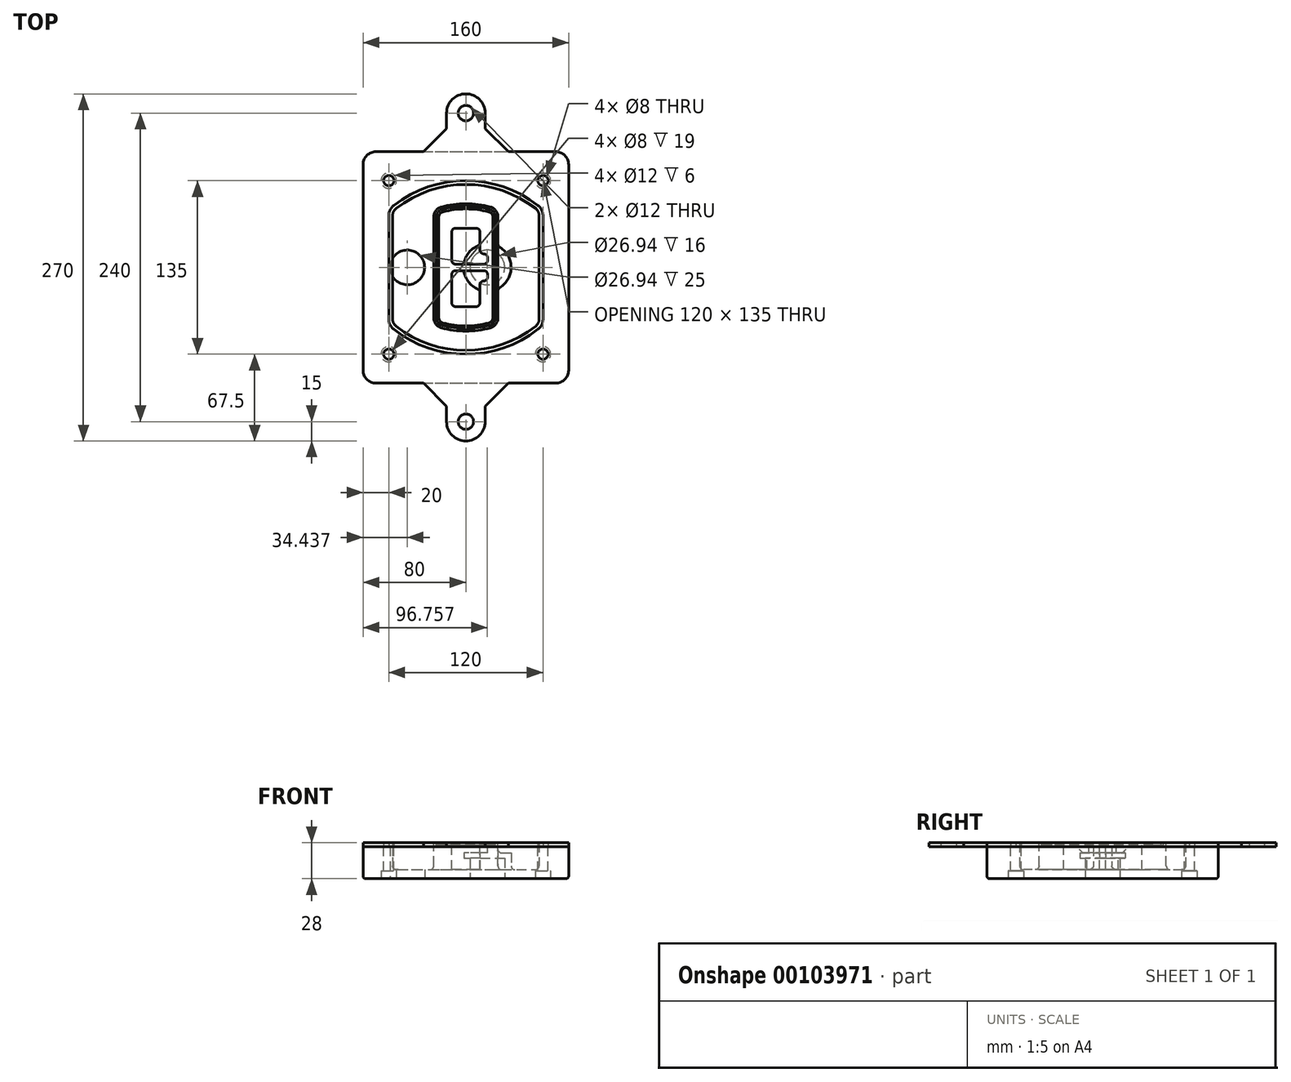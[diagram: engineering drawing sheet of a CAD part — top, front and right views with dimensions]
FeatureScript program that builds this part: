
annotation { "Feature Type Name" : "Feature", "Feature Type Description" : "" }
export const myFeature = defineFeature(function(context is Context, id is Id, definition is map)
    precondition{}
    {
        {
            var Q0;
            Q0=qCreatedBy(makeId("Top.planeOp"),FACE);
            var sketch = newSketch(context, id + "F0", { "sketchPlane" : qUnion([Q0])});
            skPoint(sketch, "E0.rect.middle", {"position": v(0, 0) * mm});
            skLineSegment(sketch, "E1.bottom", {"start": v(-70, -90) * mm, "end": v(70, -90) * mm});
            skLineSegment(sketch, "E1.top", {"start": v(-70, 90) * mm, "end": v(70, 90) * mm});
            skLineSegment(sketch, "E1.left", {"start": v(-80, -80) * mm, "end": v(-80, 80) * mm});
            skLineSegment(sketch, "E1.right", {"start": v(80, -80) * mm, "end": v(80, 80) * mm});
            skLineSegment(sketch, "E2", {"start": v(-80, 90) * mm, "end": v(80, -90) * mm, "construction": true});
            skLineSegment(sketch, "E3", {"start": v(80, 90) * mm, "end": v(-80, -90) * mm, "construction": true});
            skCircle(sketch, "E4", {"center": v(-60, 67.5) * mm, "radius": 4 * mm});
            skCircle(sketch, "E5", {"center": v(60, 67.5) * mm, "radius": 4 * mm});
            skCircle(sketch, "E6", {"center": v(60, -67.5) * mm, "radius": 4 * mm});
            skCircle(sketch, "E7", {"center": v(-60, -67.5) * mm, "radius": 4 * mm});
            skLineSegment(sketch, "E8", {"start": v(-60, 67.5) * mm, "end": v(60, 67.5) * mm, "construction": true});
            skLineSegment(sketch, "E9", {"start": v(60, 67.5) * mm, "end": v(60, -67.5) * mm, "construction": true});
            skLineSegment(sketch, "E10", {"start": v(60, -67.5) * mm, "end": v(-60, -67.5) * mm, "construction": true});
            skLineSegment(sketch, "E11", {"start": v(-60, -67.5) * mm, "end": v(-60, 67.5) * mm, "construction": true});
            skLineSegment(sketch, "E12", {"start": v(-60, 40.3) * mm, "end": v(-60, -40.3) * mm});
            skLineSegment(sketch, "E13", {"start": v(60, 40.3) * mm, "end": v(60, -40.3) * mm});
            skArc(sketch, "E14", {"start": v(56.15, 48.18) * mm, "mid": v(0, 67.5) * mm, "end": v(-56.15, 48.18) * mm});
            skArc(sketch, "E15", {"start": v(-56.15, -48.18) * mm, "mid": v(0, -67.5) * mm, "end": v(56.15, -48.18) * mm});
            skLineSegment(sketch, "E16", {"start": v(-60, 0) * mm, "end": v(60, 0) * mm, "construction": true});
            skPoint(sketch, "E17.visualSharp", {"position": v(-60, -45) * mm});
            skArc(sketch, "E17.filletArc", {"start": v(-60, -40.3) * mm, "mid": v(-58.99, -44.68) * mm, "end": v(-56.15, -48.18) * mm});
            skPoint(sketch, "E18.visualSharp", {"position": v(-60, 45) * mm});
            skArc(sketch, "E18.filletArc", {"start": v(-56.15, 48.18) * mm, "mid": v(-58.99, 44.68) * mm, "end": v(-60, 40.3) * mm});
            skPoint(sketch, "E19.visualSharp", {"position": v(60, 45) * mm});
            skArc(sketch, "E19.filletArc", {"start": v(60, 40.3) * mm, "mid": v(58.99, 44.68) * mm, "end": v(56.15, 48.18) * mm});
            skPoint(sketch, "E20.visualSharp", {"position": v(60, -45) * mm});
            skArc(sketch, "E20.filletArc", {"start": v(56.15, -48.18) * mm, "mid": v(58.99, -44.68) * mm, "end": v(60, -40.3) * mm});
            skPoint(sketch, "E21.visualSharp", {"position": v(-80, 90) * mm});
            skArc(sketch, "E21.filletArc", {"start": v(-70, 90) * mm, "mid": v(-77.07, 87.07) * mm, "end": v(-80, 80) * mm});
            skPoint(sketch, "E22.visualSharp", {"position": v(80, 90) * mm});
            skArc(sketch, "E22.filletArc", {"start": v(80, 80) * mm, "mid": v(77.07, 87.07) * mm, "end": v(70, 90) * mm});
            skPoint(sketch, "E23.visualSharp", {"position": v(80, -90) * mm});
            skArc(sketch, "E23.filletArc", {"start": v(70, -90) * mm, "mid": v(77.07, -87.07) * mm, "end": v(80, -80) * mm});
            skPoint(sketch, "E24.visualSharp", {"position": v(-80, -90) * mm});
            skArc(sketch, "E24.filletArc", {"start": v(-80, -80) * mm, "mid": v(-77.07, -87.07) * mm, "end": v(-70, -90) * mm});
            skArc(sketch, "E25.0", {"start": v(57, 40.3) * mm, "mid": v(56.3, 43.36) * mm, "end": v(54.3, 45.81) * mm});
            skLineSegment(sketch, "E25.1", {"start": v(57, 40.3) * mm, "end": v(57, -40.3) * mm});
            skArc(sketch, "E25.2", {"start": v(54.3, -45.81) * mm, "mid": v(56.3, -43.36) * mm, "end": v(57, -40.3) * mm});
            skArc(sketch, "E25.3", {"start": v(-54.3, -45.81) * mm, "mid": v(0, -64.5) * mm, "end": v(54.3, -45.81) * mm});
            skArc(sketch, "E25.4", {"start": v(-57, -40.3) * mm, "mid": v(-56.3, -43.36) * mm, "end": v(-54.3, -45.81) * mm});
            skArc(sketch, "E25.5", {"start": v(54.3, 45.81) * mm, "mid": v(0, 64.5) * mm, "end": v(-54.3, 45.81) * mm});
            skLineSegment(sketch, "E25.6", {"start": v(-57, 40.3) * mm, "end": v(-57, -40.3) * mm});
            skArc(sketch, "E25.7", {"start": v(-54.3, 45.81) * mm, "mid": v(-56.3, 43.36) * mm, "end": v(-57, 40.3) * mm});
            skArc(sketch, "E26.0", {"start": v(-58.62, 51.33) * mm, "mid": v(-62.58, 46.43) * mm, "end": v(-64, 40.3) * mm});
            skArc(sketch, "E26.1", {"start": v(58.62, 51.33) * mm, "mid": v(0, 71.5) * mm, "end": v(-58.62, 51.33) * mm});
            skArc(sketch, "E26.2", {"start": v(64, 40.3) * mm, "mid": v(62.58, 46.43) * mm, "end": v(58.62, 51.33) * mm});
            skLineSegment(sketch, "E26.3", {"start": v(64, 40.3) * mm, "end": v(64, -40.3) * mm});
            skArc(sketch, "E26.4", {"start": v(58.62, -51.33) * mm, "mid": v(62.58, -46.43) * mm, "end": v(64, -40.3) * mm});
            skLineSegment(sketch, "E26.5", {"start": v(-64, 40.3) * mm, "end": v(-64, -40.3) * mm});
            skArc(sketch, "E26.6", {"start": v(-58.62, -51.33) * mm, "mid": v(0, -71.5) * mm, "end": v(58.62, -51.33) * mm});
            skArc(sketch, "E26.7", {"start": v(-64, -40.3) * mm, "mid": v(-62.58, -46.43) * mm, "end": v(-58.62, -51.33) * mm});
            skSolve(sketch);
        }
        {
            var Q0;
            Q0=makeQuery(id+"F0.imprint","IMPRINT",FACE,{"disambiguationData":[TD([[makeQuery(id+"F0.imprint","IMPRINT",EDGE,{"derivedFrom":sQuery(id+"F0.wireOp",EDGE,"E1.bottom")}),1.0]])]});
            var Q1;
            Q1=makeQuery(id+"F0.imprint","IMPRINT",FACE,{"disambiguationData":[TD([[makeQuery(id+"F0.imprint","IMPRINT",EDGE,{"derivedFrom":sQuery(id+"F0.wireOp",EDGE,"E12")}),1.0]])]});
            var Q2;
            Q2=makeQuery(id+"F0.imprint","IMPRINT",FACE,{"disambiguationData":[TD([[makeQuery(id+"F0.imprint","IMPRINT",EDGE,{"derivedFrom":sQuery(id+"F0.wireOp",EDGE,"E25.0")}),1.0]])]});
            var Q3;
            Q3=makeQuery(id+"F0.imprint","IMPRINT",FACE,{"disambiguationData":[TD([[makeQuery(id+"F0.imprint","IMPRINT",EDGE,{"derivedFrom":sQuery(id+"F0.wireOp",EDGE,"E12")}),-1.0]])]});
            extrude(context, id + "F1", {"entities" : qUnion([Q0, Q1, Q2, Q3]), "oppositeDirection" : true, "depth" : 25 * mm});
        }
        {
            var Q0;
            Q0=makeQuery(id+"F0.imprint","IMPRINT",FACE,{"disambiguationData":[TD([[makeQuery(id+"F0.imprint","IMPRINT",EDGE,{"derivedFrom":sQuery(id+"F0.wireOp",EDGE,"E12")}),1.0]])]});
            extrude(context, id + "F2", {"entities" : qUnion([Q0]), "operationType" : NewBodyOperationType.ADD, "depth" : 3 * mm});
        }
        {
            var Q0;
            Q0=makeQuery(id+"F0.imprint","IMPRINT",FACE,{"disambiguationData":[TD([[makeQuery(id+"F0.imprint","IMPRINT",EDGE,{"derivedFrom":sQuery(id+"F0.wireOp",EDGE,"E25.0")}),1.0]])]});
            extrude(context, id + "F3", {"entities" : qUnion([Q0]), "operationType" : NewBodyOperationType.REMOVE, "oppositeDirection" : true, "depth" : 18 * mm});
        }
        {
            var Q0;
            Q0=makeQuery(id+"F2.opExtrude","CAP_FACE",FACE,{"disambiguationData":[OSD([sQuery(id+"F0.wireOp",EDGE,"E12"),sQuery(id+"F0.wireOp",EDGE,"E13"),sQuery(id+"F0.wireOp",EDGE,"E14"),sQuery(id+"F0.wireOp",EDGE,"E15"),sQuery(id+"F0.wireOp",EDGE,"E17.filletArc"),sQuery(id+"F0.wireOp",EDGE,"E18.filletArc"),sQuery(id+"F0.wireOp",EDGE,"E19.filletArc"),sQuery(id+"F0.wireOp",EDGE,"E20.filletArc"),sQuery(id+"F0.wireOp",EDGE,"E25.0"),sQuery(id+"F0.wireOp",EDGE,"E25.1"),sQuery(id+"F0.wireOp",EDGE,"E25.2"),sQuery(id+"F0.wireOp",EDGE,"E25.3"),sQuery(id+"F0.wireOp",EDGE,"E25.4"),sQuery(id+"F0.wireOp",EDGE,"E25.5"),sQuery(id+"F0.wireOp",EDGE,"E25.6"),sQuery(id+"F0.wireOp",EDGE,"E25.7")])],"isStart":false});
            var sketch = newSketch(context, id + "F4", { "sketchPlane" : qUnion([Q0])});
            skArc(sketch, "E27.0", {"start": v(-19.08, -46.97) * mm, "mid": v(0, -49.5) * mm, "end": v(19.08, -46.97) * mm});
            skArc(sketch, "E28.0", {"start": v(19.08, 46.97) * mm, "mid": v(0, 49.5) * mm, "end": v(-19.08, 46.97) * mm});
            skLineSegment(sketch, "E29", {"start": v(-25, 39.25) * mm, "end": v(-25, -39.25) * mm});
            skLineSegment(sketch, "E30", {"start": v(25, 39.25) * mm, "end": v(25, -39.25) * mm});
            skLineSegment(sketch, "E31", {"start": v(-25, 45.1) * mm, "end": v(25, 45.1) * mm, "construction": true});
            skLineSegment(sketch, "E32", {"start": v(-25, -45.1) * mm, "end": v(25, -45.1) * mm, "construction": true});
            skPoint(sketch, "E33.visualSharp", {"position": v(-25, 45.1) * mm});
            skArc(sketch, "E33.filletArc", {"start": v(-19.08, 46.97) * mm, "mid": v(-23.35, 44.11) * mm, "end": v(-25, 39.25) * mm});
            skPoint(sketch, "E34.visualSharp", {"position": v(25, 45.1) * mm});
            skArc(sketch, "E34.filletArc", {"start": v(25, 39.25) * mm, "mid": v(23.35, 44.11) * mm, "end": v(19.08, 46.97) * mm});
            skPoint(sketch, "E35.visualSharp", {"position": v(25, -45.1) * mm});
            skArc(sketch, "E35.filletArc", {"start": v(19.08, -46.97) * mm, "mid": v(23.35, -44.11) * mm, "end": v(25, -39.25) * mm});
            skPoint(sketch, "E36.visualSharp", {"position": v(-25, -45.1) * mm});
            skArc(sketch, "E36.filletArc", {"start": v(-25, -39.25) * mm, "mid": v(-23.35, -44.11) * mm, "end": v(-19.08, -46.97) * mm});
            skArc(sketch, "E37.0", {"start": v(54.3, 45.81) * mm, "mid": v(0, 64.5) * mm, "end": v(-54.3, 45.81) * mm});
            skArc(sketch, "E37.1", {"start": v(-54.3, 45.81) * mm, "mid": v(-56.3, 43.36) * mm, "end": v(-57, 40.3) * mm});
            skLineSegment(sketch, "E37.2", {"start": v(-57, 40.3) * mm, "end": v(-57, -40.3) * mm});
            skArc(sketch, "E37.3", {"start": v(-57, -40.3) * mm, "mid": v(-56.3, -43.36) * mm, "end": v(-54.3, -45.81) * mm});
            skArc(sketch, "E37.4", {"start": v(-54.3, -45.81) * mm, "mid": v(0, -64.5) * mm, "end": v(54.3, -45.81) * mm});
            skArc(sketch, "E37.5", {"start": v(54.3, -45.81) * mm, "mid": v(56.3, -43.36) * mm, "end": v(57, -40.3) * mm});
            skLineSegment(sketch, "E37.6", {"start": v(57, 40.3) * mm, "end": v(57, -40.3) * mm});
            skArc(sketch, "E37.7", {"start": v(57, 40.3) * mm, "mid": v(56.3, 43.36) * mm, "end": v(54.3, 45.81) * mm});
            skLineSegment(sketch, "E38.0", {"start": v(23, 39.25) * mm, "end": v(23, -39.25) * mm});
            skArc(sketch, "E38.1", {"start": v(18.56, -45.04) * mm, "mid": v(21.76, -42.9) * mm, "end": v(23, -39.25) * mm});
            skArc(sketch, "E38.2", {"start": v(-18.56, -45.04) * mm, "mid": v(0, -47.5) * mm, "end": v(18.56, -45.04) * mm});
            skArc(sketch, "E38.3", {"start": v(-23, -39.25) * mm, "mid": v(-21.76, -42.9) * mm, "end": v(-18.56, -45.04) * mm});
            skLineSegment(sketch, "E38.4", {"start": v(-23, 39.25) * mm, "end": v(-23, -39.25) * mm});
            skArc(sketch, "E38.5", {"start": v(23, 39.25) * mm, "mid": v(21.76, 42.9) * mm, "end": v(18.56, 45.04) * mm});
            skArc(sketch, "E38.6", {"start": v(-18.56, 45.04) * mm, "mid": v(-21.76, 42.9) * mm, "end": v(-23, 39.25) * mm});
            skArc(sketch, "E38.7", {"start": v(18.56, 45.04) * mm, "mid": v(0, 47.5) * mm, "end": v(-18.56, 45.04) * mm});
            skArc(sketch, "E39.0", {"start": v(21, 39.25) * mm, "mid": v(20.18, 41.68) * mm, "end": v(18.04, 43.1) * mm});
            skLineSegment(sketch, "E39.1", {"start": v(21, 39.25) * mm, "end": v(21, -39.25) * mm});
            skArc(sketch, "E39.2", {"start": v(18.04, -43.1) * mm, "mid": v(20.18, -41.68) * mm, "end": v(21, -39.25) * mm});
            skArc(sketch, "E39.3", {"start": v(-18.04, -43.1) * mm, "mid": v(0, -45.5) * mm, "end": v(18.04, -43.1) * mm});
            skArc(sketch, "E39.4", {"start": v(-21, -39.25) * mm, "mid": v(-20.18, -41.68) * mm, "end": v(-18.04, -43.1) * mm});
            skArc(sketch, "E39.5", {"start": v(18.04, 43.1) * mm, "mid": v(0, 45.5) * mm, "end": v(-18.04, 43.1) * mm});
            skLineSegment(sketch, "E39.6", {"start": v(-21, 39.25) * mm, "end": v(-21, -39.25) * mm});
            skArc(sketch, "E39.7", {"start": v(-18.04, 43.1) * mm, "mid": v(-20.18, 41.68) * mm, "end": v(-21, 39.25) * mm});
            skLineSegment(sketch, "E40", {"start": v(-25, 0) * mm, "end": v(25, 0) * mm, "construction": true});
            skLineSegment(sketch, "E41", {"start": v(-11, 5.5) * mm, "end": v(-11, 27.5) * mm});
            skLineSegment(sketch, "E42", {"start": v(-8, 30.5) * mm, "end": v(8, 30.5) * mm});
            skLineSegment(sketch, "E43", {"start": v(11, 27.5) * mm, "end": v(11, 13.5) * mm});
            skLineSegment(sketch, "E44", {"start": v(14, 10.5) * mm, "end": v(14, 10.5) * mm});
            skLineSegment(sketch, "E45", {"start": v(17, 7.5) * mm, "end": v(17, 5.5) * mm});
            skLineSegment(sketch, "E46", {"start": v(14, 2.5) * mm, "end": v(-8, 2.5) * mm});
            skPoint(sketch, "E47.visualSharp", {"position": v(-11, 30.5) * mm});
            skArc(sketch, "E47.filletArc", {"start": v(-8, 30.5) * mm, "mid": v(-10.12, 29.62) * mm, "end": v(-11, 27.5) * mm});
            skPoint(sketch, "E48.visualSharp", {"position": v(11, 30.5) * mm});
            skArc(sketch, "E48.filletArc", {"start": v(11, 27.5) * mm, "mid": v(10.12, 29.62) * mm, "end": v(8, 30.5) * mm});
            skPoint(sketch, "E49.visualSharp", {"position": v(11, 10.5) * mm});
            skArc(sketch, "E49.filletArc", {"start": v(11, 13.5) * mm, "mid": v(11.88, 11.38) * mm, "end": v(14, 10.5) * mm});
            skPoint(sketch, "E50.visualSharp", {"position": v(17, 10.5) * mm});
            skArc(sketch, "E50.filletArc", {"start": v(17, 7.5) * mm, "mid": v(16.12, 9.62) * mm, "end": v(14, 10.5) * mm});
            skPoint(sketch, "E51.visualSharp", {"position": v(17, 2.5) * mm});
            skArc(sketch, "E51.filletArc", {"start": v(14, 2.5) * mm, "mid": v(16.12, 3.38) * mm, "end": v(17, 5.5) * mm});
            skPoint(sketch, "E52.visualSharp", {"position": v(-11, 2.5) * mm});
            skArc(sketch, "E52.filletArc", {"start": v(-11, 5.5) * mm, "mid": v(-10.12, 3.38) * mm, "end": v(-8, 2.5) * mm});
            skLineSegment(sketch, "E53.0.MirrorCS", {"start": v(14, -2.5) * mm, "end": v(-8, -2.5) * mm});
            skArc(sketch, "E54.0.MirrorCS", {"start": v(-11, -5.5) * mm, "mid": v(-10.12, -3.38) * mm, "end": v(-8, -2.5) * mm});
            skLineSegment(sketch, "E55.0.MirrorCS", {"start": v(-11, -5.5) * mm, "end": v(-11, -27.5) * mm});
            skArc(sketch, "E56.0.MirrorCS", {"start": v(-8, -30.5) * mm, "mid": v(-10.12, -29.62) * mm, "end": v(-11, -27.5) * mm});
            skLineSegment(sketch, "E57.0.MirrorCS", {"start": v(-8, -30.5) * mm, "end": v(8, -30.5) * mm});
            skArc(sketch, "E58.0.MirrorCS", {"start": v(11, -27.5) * mm, "mid": v(10.12, -29.62) * mm, "end": v(8, -30.5) * mm});
            skLineSegment(sketch, "E59.0.MirrorCS", {"start": v(11, -27.5) * mm, "end": v(11, -13.5) * mm});
            skArc(sketch, "E60.0.MirrorCS", {"start": v(11, -13.5) * mm, "mid": v(11.88, -11.38) * mm, "end": v(14, -10.5) * mm});
            skArc(sketch, "E61.0.MirrorCS", {"start": v(17, -7.5) * mm, "mid": v(16.12, -9.62) * mm, "end": v(14, -10.5) * mm});
            skLineSegment(sketch, "E62.0.MirrorCS", {"start": v(17, -7.5) * mm, "end": v(17, -5.5) * mm});
            skArc(sketch, "E63.0.MirrorCS", {"start": v(14, -2.5) * mm, "mid": v(16.12, -3.38) * mm, "end": v(17, -5.5) * mm});
            skSolve(sketch);
        }
        {
            var Q0;
            Q0=makeQuery(id+"F4.imprint","IMPRINT",FACE,{"disambiguationData":[TD([[makeQuery(id+"F4.imprint","IMPRINT",EDGE,{"derivedFrom":sQuery(id+"F4.wireOp",EDGE,"E27.0")}),1.0]])]});
            var Q1;
            Q1=makeQuery(id+"F4.imprint","IMPRINT",FACE,{"disambiguationData":[TD([[makeQuery(id+"F4.imprint","IMPRINT",EDGE,{"derivedFrom":sQuery(id+"F4.wireOp",EDGE,"E38.0")}),-1.0]])]});
            var Q2;
            Q2=makeQuery(id+"F4.imprint","IMPRINT",FACE,{"disambiguationData":[TD([[makeQuery(id+"F4.imprint","IMPRINT",EDGE,{"derivedFrom":sQuery(id+"F4.wireOp",EDGE,"E39.0")}),1.0]])]});
            extrude(context, id + "F5", {"entities" : qUnion([Q0, Q1, Q2]), "operationType" : NewBodyOperationType.ADD, "endBound" : BoundingType.UP_TO_NEXT, "oppositeDirection" : true, "depth" : 25 * mm});
        }
        {
            var Q0;
            Q0=makeQuery(id+"F4.imprint","IMPRINT",FACE,{"disambiguationData":[TD([[makeQuery(id+"F4.imprint","IMPRINT",EDGE,{"derivedFrom":sQuery(id+"F4.wireOp",EDGE,"E38.0")}),-1.0]])]});
            extrude(context, id + "F6", {"entities" : qUnion([Q0]), "operationType" : NewBodyOperationType.REMOVE, "oppositeDirection" : true, "depth" : 2 * mm});
        }
        {
            var Q0;
            Q0=makeQuery(id+"F1.opExtrude","CAP_FACE",FACE,{"disambiguationData":[OSD([sQuery(id+"F0.wireOp",EDGE,"E1.bottom"),sQuery(id+"F0.wireOp",EDGE,"E1.top"),sQuery(id+"F0.wireOp",EDGE,"E1.left"),sQuery(id+"F0.wireOp",EDGE,"E1.right"),sQuery(id+"F0.wireOp",EDGE,"E4"),sQuery(id+"F0.wireOp",EDGE,"E5"),sQuery(id+"F0.wireOp",EDGE,"E6"),sQuery(id+"F0.wireOp",EDGE,"E7"),sQuery(id+"F0.wireOp",EDGE,"E21.filletArc"),sQuery(id+"F0.wireOp",EDGE,"E22.filletArc"),sQuery(id+"F0.wireOp",EDGE,"E23.filletArc"),sQuery(id+"F0.wireOp",EDGE,"E24.filletArc")])],"isStart":false});
            var sketch = newSketch(context, id + "F7", { "sketchPlane" : qUnion([Q0])});
            skCircle(sketch, "E64", {"center": v(16.76, 0) * mm, "radius": 13.47 * mm});
            skCircle(sketch, "E65", {"center": v(-45.56, 0) * mm, "radius": 13.47 * mm});
            skLineSegment(sketch, "E66", {"start": v(80, 0) * mm, "end": v(-80, 0) * mm});
            skCircle(sketch, "E67", {"center": v(16.76, 0) * mm, "radius": 18.47 * mm});
            skCircle(sketch, "E68", {"center": v(60, -67.5) * mm, "radius": 6 * mm});
            skCircle(sketch, "E69", {"center": v(-60, -67.5) * mm, "radius": 6 * mm});
            skCircle(sketch, "E70", {"center": v(-60, 67.5) * mm, "radius": 6 * mm});
            skCircle(sketch, "E71", {"center": v(60, 67.5) * mm, "radius": 6 * mm});
            skSolve(sketch);
        }
        {
            var Q0;
            {var subQ1=sQuery(id+"F7.wireOp",EDGE,"E66");var subQ4=sQuery(id+"F7.wireOp",EDGE,"E64");var subQ6=makeQuery(id+"F7.imprint","INTERSECT",VERTEX,{"disambiguationData":[OD(0.0)],"derivedFrom":[subQ4,subQ1]});Q0=makeQuery(id+"F7.imprint","IMPRINT",FACE,{"disambiguationData":[TD([[makeQuery(id+"F7.imprint","IMPRINT",EDGE,{"disambiguationData":[TD([[subQ6,-1.0]])],"derivedFrom":subQ4}),-1.0]])]});}
            var Q1;
            {var subQ0=sQuery(id+"F7.wireOp",EDGE,"E66");var subQ1=sQuery(id+"F7.wireOp",EDGE,"E64");var subQ3=makeQuery(id+"F7.imprint","INTERSECT",VERTEX,{"disambiguationData":[OD(0.0)],"derivedFrom":[subQ1,subQ0]});Q1=makeQuery(id+"F7.imprint","IMPRINT",FACE,{"disambiguationData":[TD([[makeQuery(id+"F7.imprint","IMPRINT",EDGE,{"disambiguationData":[TD([[subQ3,-1.0]])],"derivedFrom":subQ1}),1.0]])]});}
            var Q2;
            {var subQ0=sQuery(id+"F7.wireOp",EDGE,"E66");var subQ1=sQuery(id+"F7.wireOp",EDGE,"E64");var subQ3=makeQuery(id+"F7.imprint","INTERSECT",VERTEX,{"disambiguationData":[OD(0.0)],"derivedFrom":[subQ1,subQ0]});Q2=makeQuery(id+"F7.imprint","IMPRINT",FACE,{"disambiguationData":[TD([[makeQuery(id+"F7.imprint","IMPRINT",EDGE,{"disambiguationData":[TD([[subQ3,1.0]])],"derivedFrom":subQ1}),1.0]])]});}
            var Q3;
            {var subQ1=sQuery(id+"F7.wireOp",EDGE,"E66");var subQ4=sQuery(id+"F7.wireOp",EDGE,"E64");var subQ6=makeQuery(id+"F7.imprint","INTERSECT",VERTEX,{"disambiguationData":[OD(0.0)],"derivedFrom":[subQ4,subQ1]});Q3=makeQuery(id+"F7.imprint","IMPRINT",FACE,{"disambiguationData":[TD([[makeQuery(id+"F7.imprint","IMPRINT",EDGE,{"disambiguationData":[TD([[subQ6,1.0]])],"derivedFrom":subQ4}),-1.0]])]});}
            extrude(context, id + "F8", {"entities" : qUnion([Q0, Q1, Q2, Q3]), "operationType" : NewBodyOperationType.ADD, "oppositeDirection" : true, "depth" : 20 * mm});
        }
        {
            var Q0;
            {var subQ0=sQuery(id+"F7.wireOp",EDGE,"E66");var subQ1=sQuery(id+"F7.wireOp",EDGE,"E64");var subQ3=makeQuery(id+"F7.imprint","INTERSECT",VERTEX,{"disambiguationData":[OD(0.0)],"derivedFrom":[subQ1,subQ0]});Q0=makeQuery(id+"F7.imprint","IMPRINT",FACE,{"disambiguationData":[TD([[makeQuery(id+"F7.imprint","IMPRINT",EDGE,{"disambiguationData":[TD([[subQ3,-1.0]])],"derivedFrom":subQ1}),1.0]])]});}
            var Q1;
            {var subQ0=sQuery(id+"F7.wireOp",EDGE,"E66");var subQ1=sQuery(id+"F7.wireOp",EDGE,"E64");var subQ3=makeQuery(id+"F7.imprint","INTERSECT",VERTEX,{"disambiguationData":[OD(0.0)],"derivedFrom":[subQ1,subQ0]});Q1=makeQuery(id+"F7.imprint","IMPRINT",FACE,{"disambiguationData":[TD([[makeQuery(id+"F7.imprint","IMPRINT",EDGE,{"disambiguationData":[TD([[subQ3,1.0]])],"derivedFrom":subQ1}),1.0]])]});}
            extrude(context, id + "F9", {"entities" : qUnion([Q0, Q1]), "operationType" : NewBodyOperationType.REMOVE, "oppositeDirection" : true, "depth" : 16 * mm});
        }
        {
            var Q0;
            {var subQ0=sQuery(id+"F7.wireOp",EDGE,"E66");var subQ1=sQuery(id+"F7.wireOp",EDGE,"E65");var subQ3=makeQuery(id+"F7.imprint","INTERSECT",VERTEX,{"disambiguationData":[OD(0.0)],"derivedFrom":[subQ1,subQ0]});Q0=makeQuery(id+"F7.imprint","IMPRINT",FACE,{"disambiguationData":[TD([[makeQuery(id+"F7.imprint","IMPRINT",EDGE,{"disambiguationData":[TD([[subQ3,-1.0]])],"derivedFrom":subQ1}),1.0]])]});}
            var Q1;
            {var subQ0=sQuery(id+"F7.wireOp",EDGE,"E66");var subQ1=sQuery(id+"F7.wireOp",EDGE,"E65");var subQ3=makeQuery(id+"F7.imprint","INTERSECT",VERTEX,{"disambiguationData":[OD(0.0)],"derivedFrom":[subQ1,subQ0]});Q1=makeQuery(id+"F7.imprint","IMPRINT",FACE,{"disambiguationData":[TD([[makeQuery(id+"F7.imprint","IMPRINT",EDGE,{"disambiguationData":[TD([[subQ3,1.0]])],"derivedFrom":subQ1}),1.0]])]});}
            extrude(context, id + "F10", {"entities" : qUnion([Q0, Q1]), "operationType" : NewBodyOperationType.REMOVE, "oppositeDirection" : true, "depth" : 25 * mm});
        }
        {
            var Q0;
            Q0=makeQuery(id+"F7.imprint","IMPRINT",FACE,{"disambiguationData":[TD([[makeQuery(id+"F7.imprint","IMPRINT",EDGE,{"derivedFrom":sQuery(id+"F7.wireOp",EDGE,"E68")}),1.0]])]});
            var Q1;
            Q1=makeQuery(id+"F7.imprint","IMPRINT",FACE,{"disambiguationData":[TD([[makeQuery(id+"F7.imprint","IMPRINT",EDGE,{"derivedFrom":makeQuery(id+"F1.opExtrude","CAP_EDGE",EDGE,{"disambiguationData":[OSD([sQuery(id+"F0.wireOp",EDGE,"E5")])],"isStart":false})}),-1.0]])]});
            var Q2;
            Q2=makeQuery(id+"F7.imprint","IMPRINT",FACE,{"disambiguationData":[TD([[makeQuery(id+"F7.imprint","IMPRINT",EDGE,{"derivedFrom":sQuery(id+"F7.wireOp",EDGE,"E69")}),1.0]])]});
            var Q3;
            Q3=makeQuery(id+"F7.imprint","IMPRINT",FACE,{"disambiguationData":[TD([[makeQuery(id+"F7.imprint","IMPRINT",EDGE,{"derivedFrom":makeQuery(id+"F1.opExtrude","CAP_EDGE",EDGE,{"disambiguationData":[OSD([sQuery(id+"F0.wireOp",EDGE,"E4")])],"isStart":false})}),-1.0]])]});
            var Q4;
            Q4=makeQuery(id+"F7.imprint","IMPRINT",FACE,{"disambiguationData":[TD([[makeQuery(id+"F7.imprint","IMPRINT",EDGE,{"derivedFrom":sQuery(id+"F7.wireOp",EDGE,"E70")}),1.0]])]});
            var Q5;
            Q5=makeQuery(id+"F7.imprint","IMPRINT",FACE,{"disambiguationData":[TD([[makeQuery(id+"F7.imprint","IMPRINT",EDGE,{"derivedFrom":makeQuery(id+"F1.opExtrude","CAP_EDGE",EDGE,{"disambiguationData":[OSD([sQuery(id+"F0.wireOp",EDGE,"E7")])],"isStart":false})}),-1.0]])]});
            var Q6;
            Q6=makeQuery(id+"F7.imprint","IMPRINT",FACE,{"disambiguationData":[TD([[makeQuery(id+"F7.imprint","IMPRINT",EDGE,{"derivedFrom":sQuery(id+"F7.wireOp",EDGE,"E71")}),1.0]])]});
            var Q7;
            Q7=makeQuery(id+"F7.imprint","IMPRINT",FACE,{"disambiguationData":[TD([[makeQuery(id+"F7.imprint","IMPRINT",EDGE,{"derivedFrom":makeQuery(id+"F1.opExtrude","CAP_EDGE",EDGE,{"disambiguationData":[OSD([sQuery(id+"F0.wireOp",EDGE,"E6")])],"isStart":false})}),-1.0]])]});
            extrude(context, id + "F11", {"entities" : qUnion([Q0, Q1, Q2, Q3, Q4, Q5, Q6, Q7]), "operationType" : NewBodyOperationType.REMOVE, "oppositeDirection" : true, "depth" : 6 * mm});
        }
        {
            var Q0;
            Q0=makeQuery(id+"F9.boolean.opBoolean","COPY",FACE,{"derivedFrom":makeQuery(id+"F9.opExtrude","CAP_FACE",FACE,{"disambiguationData":[OSD([sQuery(id+"F7.wireOp",EDGE,"E64")])],"isStart":false})});
            var sketch = newSketch(context, id + "F12", { "sketchPlane" : qUnion([Q0])});
            skArc(sketch, "E72.0", {"start": v(11, 17.55) * mm, "mid": v(2.57, 11.82) * mm, "end": v(-1.54, 2.5) * mm});
            skArc(sketch, "E72.1", {"start": v(-1.54, -2.5) * mm, "mid": v(2.57, -11.82) * mm, "end": v(11, -17.55) * mm});
            skLineSegment(sketch, "E73", {"start": v(-1.54, -2.5) * mm, "end": v(14, -2.5) * mm});
            skLineSegment(sketch, "E74.0", {"start": v(14, 2.5) * mm, "end": v(-1.54, 2.5) * mm});
            skArc(sketch, "E74.1", {"start": v(14, 2.5) * mm, "mid": v(16.12, 3.38) * mm, "end": v(17, 5.5) * mm});
            skLineSegment(sketch, "E74.2", {"start": v(17, 7.5) * mm, "end": v(17, 5.5) * mm});
            skArc(sketch, "E74.3", {"start": v(17, 7.5) * mm, "mid": v(16.12, 9.62) * mm, "end": v(14, 10.5) * mm});
            skArc(sketch, "E74.4", {"start": v(11, 13.5) * mm, "mid": v(11.88, 11.38) * mm, "end": v(14, 10.5) * mm});
            skLineSegment(sketch, "E74.5", {"start": v(11, 17.55) * mm, "end": v(11, 13.5) * mm});
            skLineSegment(sketch, "E74.7", {"start": v(14, -2.5) * mm, "end": v(-1.54, -2.5) * mm});
            skArc(sketch, "E74.8", {"start": v(14, -2.5) * mm, "mid": v(16.12, -3.38) * mm, "end": v(17, -5.5) * mm});
            skLineSegment(sketch, "E74.9", {"start": v(17, -7.5) * mm, "end": v(17, -5.5) * mm});
            skArc(sketch, "E74.10", {"start": v(17, -7.5) * mm, "mid": v(16.12, -9.62) * mm, "end": v(14, -10.5) * mm});
            skArc(sketch, "E74.11", {"start": v(11, -13.5) * mm, "mid": v(11.88, -11.38) * mm, "end": v(14, -10.5) * mm});
            skLineSegment(sketch, "E74.12", {"start": v(11, -17.55) * mm, "end": v(11, -13.5) * mm});
            skPoint(sketch, "E75.orphan", {"position": v(11, -27.5) * mm});
            skPoint(sketch, "E76.orphan", {"position": v(-8, -2.5) * mm});
            skPoint(sketch, "E77.orphan", {"position": v(-8, 2.5) * mm});
            skPoint(sketch, "E78.orphan", {"position": v(11, 27.5) * mm});
            skSolve(sketch);
        }
        {
            var Q0;
            {var subQ7=sQuery(id+"F12.wireOp",EDGE,"E72.0");var subQ14=sQuery(id+"F12.wireOp",EDGE,"E72.1");var subQ16=sQuery(id+"F12.wireOp",EDGE,"E74.1");var subQ18=sQuery(id+"F12.wireOp",EDGE,"E74.8");Q0=qUnion([makeQuery(id+"F12.imprint","IMPRINT",FACE,{"disambiguationData":[TD([[makeQuery(id+"F12.imprint","IMPRINT",EDGE,{"derivedFrom":subQ7}),1.0]])]}),makeQuery(id+"F12.imprint","IMPRINT",FACE,{"disambiguationData":[TD([[makeQuery(id+"F12.imprint","IMPRINT",EDGE,{"derivedFrom":subQ14}),1.0]])]}),makeQuery(id+"F12.imprint","IMPRINT",FACE,{"disambiguationData":[TD([[makeQuery(id+"F12.imprint","IMPRINT",EDGE,{"derivedFrom":subQ16}),1.0]])]}),makeQuery(id+"F12.imprint","IMPRINT",FACE,{"disambiguationData":[TD([[makeQuery(id+"F12.imprint","IMPRINT",EDGE,{"derivedFrom":subQ18}),-1.0]])]})]);}
            var Q1;
            Q1=makeQuery(id+"F5.boolean.opBoolean","SPLIT",FACE,{"disambiguationData":[TD([makeQuery(id+"F5.opExtrude","SWEPT_FACE",FACE,{"disambiguationData":[OSD([sQuery(id+"F4.wireOp",EDGE,"E41")])]})])],"derivedFrom":makeQuery(id+"F3.boolean.opBoolean","COPY",FACE,{"derivedFrom":makeQuery(id+"F3.opExtrude","CAP_FACE",FACE,{"disambiguationData":[OSD([sQuery(id+"F0.wireOp",EDGE,"E25.0"),sQuery(id+"F0.wireOp",EDGE,"E25.1"),sQuery(id+"F0.wireOp",EDGE,"E25.2"),sQuery(id+"F0.wireOp",EDGE,"E25.3"),sQuery(id+"F0.wireOp",EDGE,"E25.4"),sQuery(id+"F0.wireOp",EDGE,"E25.5"),sQuery(id+"F0.wireOp",EDGE,"E25.6"),sQuery(id+"F0.wireOp",EDGE,"E25.7")])],"isStart":false})})});
            extrude(context, id + "F13", {"entities" : qUnion([Q0]), "operationType" : NewBodyOperationType.REMOVE, "endBound" : BoundingType.UP_TO_SURFACE, "endBoundEntityFace" : qUnion([Q1]), "depth" : 25 * mm});
        }
        {
            var Q0;
            Q0=makeQuery(id+"F3.boolean.opBoolean","COPY",EDGE,{"derivedFrom":makeQuery(id+"F3.opExtrude","CAP_EDGE",EDGE,{"disambiguationData":[OSD([sQuery(id+"F0.wireOp",EDGE,"E25.6")])],"isStart":false})});
            var Q1;
            Q1=makeQuery(id+"F8.boolean.opBoolean","INTERSECT",EDGE,{"derivedFrom":[makeQuery(id+"F5.opExtrude","SWEPT_FACE",FACE,{"disambiguationData":[OSD([sQuery(id+"F4.wireOp",EDGE,"E30")])]}),makeQuery(id+"F8.opExtrude","CAP_FACE",FACE,{"disambiguationData":[OSD([sQuery(id+"F7.wireOp",EDGE,"E67")])],"isStart":false})]});
            var Q2;
            Q2=makeQuery(id+"F8.boolean.opBoolean","INTERSECT",EDGE,{"disambiguationData":[OD(1.0)],"derivedFrom":[makeQuery(id+"F5.opExtrude","SWEPT_FACE",FACE,{"disambiguationData":[OSD([sQuery(id+"F4.wireOp",EDGE,"E30")])]}),makeQuery(id+"F8.opExtrude","SWEPT_FACE",FACE,{"disambiguationData":[OSD([sQuery(id+"F7.wireOp",EDGE,"E67")])]})]});
            var Q3;
            {var subQ0=sQuery(id+"F4.wireOp",EDGE,"E30");Q3=makeQuery(id+"F8.boolean.opBoolean","SPLIT",EDGE,{"disambiguationData":[TD([makeQuery(id+"F5.opExtrude","SWEPT_FACE",FACE,{"disambiguationData":[OSD([sQuery(id+"F4.wireOp",EDGE,"E35.filletArc")])]})])],"derivedFrom":makeQuery(id+"F5.opExtrude","CAP_EDGE",EDGE,{"disambiguationData":[OSD([subQ0])],"isStart":false})});}
            var Q4;
            {var subQ0=sQuery(id+"F0.wireOp",EDGE,"E25.7");var subQ1=sQuery(id+"F0.wireOp",EDGE,"E25.1");var subQ2=sQuery(id+"F0.wireOp",EDGE,"E25.6");var subQ3=sQuery(id+"F0.wireOp",EDGE,"E25.5");var subQ4=sQuery(id+"F0.wireOp",EDGE,"E25.4");var subQ5=sQuery(id+"F0.wireOp",EDGE,"E25.0");var subQ6=sQuery(id+"F0.wireOp",EDGE,"E25.2");var subQ7=sQuery(id+"F0.wireOp",EDGE,"E25.3");Q4=makeQuery(id+"F8.boolean.opBoolean","INTERSECT",EDGE,{"derivedFrom":[makeQuery(id+"F5.boolean.opBoolean","SPLIT",FACE,{"disambiguationData":[TD([makeQuery(id+"F2.opExtrude","SWEPT_FACE",FACE,{"disambiguationData":[OSD([subQ5])]})])],"derivedFrom":makeQuery(id+"F3.boolean.opBoolean","COPY",FACE,{"derivedFrom":makeQuery(id+"F3.opExtrude","CAP_FACE",FACE,{"disambiguationData":[OSD([subQ5,subQ1,subQ6,subQ7,subQ4,subQ3,subQ2,subQ0])],"isStart":false})})}),makeQuery(id+"F8.opExtrude","SWEPT_FACE",FACE,{"disambiguationData":[OSD([sQuery(id+"F7.wireOp",EDGE,"E67")])]})]});}
            var Q5;
            Q5=makeQuery(id+"F8.boolean.opBoolean","INTERSECT",EDGE,{"disambiguationData":[OD(0.0)],"derivedFrom":[makeQuery(id+"F5.opExtrude","SWEPT_FACE",FACE,{"disambiguationData":[OSD([sQuery(id+"F4.wireOp",EDGE,"E30")])]}),makeQuery(id+"F8.opExtrude","SWEPT_FACE",FACE,{"disambiguationData":[OSD([sQuery(id+"F7.wireOp",EDGE,"E67")])]})]});
            fillet(context, id + "F14", {"entities" : qUnion([Q0, Q1, Q2, Q3, Q4, Q5]), "radius" : 3 * mm, "tangentPropagation" : true, "allowEdgeOverflow" : false});
        }
        {
            var Q0;
            Q0=makeQuery(id+"F1.opExtrude","CAP_EDGE",EDGE,{"disambiguationData":[OSD([sQuery(id+"F0.wireOp",EDGE,"E1.bottom")])],"isStart":false});
            fillet(context, id + "F15", {"entities" : qUnion([Q0]), "radius" : 2 * mm, "tangentPropagation" : true, "allowEdgeOverflow" : false});
        }
        {
            var Q0;
            {var subQ0=sQuery(id+"F0.wireOp",EDGE,"E22.filletArc");var subQ1=sQuery(id+"F0.wireOp",EDGE,"E7");var subQ2=sQuery(id+"F0.wireOp",EDGE,"E6");var subQ3=sQuery(id+"F0.wireOp",EDGE,"E5");var subQ4=sQuery(id+"F0.wireOp",EDGE,"E4");var subQ5=sQuery(id+"F0.wireOp",EDGE,"E1.bottom");var subQ6=sQuery(id+"F0.wireOp",EDGE,"E21.filletArc");var subQ7=sQuery(id+"F0.wireOp",EDGE,"E1.top");var subQ8=sQuery(id+"F0.wireOp",EDGE,"E1.left");var subQ9=sQuery(id+"F0.wireOp",EDGE,"E1.right");var subQ10=sQuery(id+"F0.wireOp",EDGE,"E23.filletArc");var subQ11=sQuery(id+"F0.wireOp",EDGE,"E24.filletArc");Q0=makeQuery(id+"F2.boolean.opBoolean","SPLIT",FACE,{"disambiguationData":[TD([makeQuery(id+"F1.opExtrude","SWEPT_FACE",FACE,{"disambiguationData":[OSD([subQ5])]})])],"derivedFrom":makeQuery(id+"F1.opExtrude","CAP_FACE",FACE,{"disambiguationData":[OSD([subQ5,subQ7,subQ8,subQ9,subQ4,subQ3,subQ2,subQ1,subQ6,subQ0,subQ10,subQ11])],"isStart":true})});}
            var sketch = newSketch(context, id + "F16", { "sketchPlane" : qUnion([Q0])});
            skLineSegment(sketch, "E79.0", {"start": v(-70, 90) * mm, "end": v(70, 90) * mm});
            skArc(sketch, "E79.1", {"start": v(-70, 90) * mm, "mid": v(-77.07, 87.07) * mm, "end": v(-80, 80) * mm});
            skLineSegment(sketch, "E79.2", {"start": v(-80, -80) * mm, "end": v(-80, 80) * mm});
            skArc(sketch, "E79.3", {"start": v(-80, -80) * mm, "mid": v(-77.07, -87.07) * mm, "end": v(-70, -90) * mm});
            skLineSegment(sketch, "E79.4", {"start": v(-70, -90) * mm, "end": v(70, -90) * mm});
            skArc(sketch, "E79.5", {"start": v(70, -90) * mm, "mid": v(77.07, -87.07) * mm, "end": v(80, -80) * mm});
            skLineSegment(sketch, "E79.6", {"start": v(80, -80) * mm, "end": v(80, 80) * mm});
            skCircle(sketch, "E79.7", {"center": v(60, -67.5) * mm, "radius": 4 * mm});
            skCircle(sketch, "E79.8", {"center": v(-60, -67.5) * mm, "radius": 4 * mm});
            skCircle(sketch, "E79.9", {"center": v(-60, 67.5) * mm, "radius": 4 * mm});
            skCircle(sketch, "E79.10", {"center": v(60, 67.5) * mm, "radius": 4 * mm});
            skArc(sketch, "E79.11", {"start": v(80, 80) * mm, "mid": v(77.07, 87.07) * mm, "end": v(70, 90) * mm});
            skArc(sketch, "E79.12", {"start": v(56.15, 48.18) * mm, "mid": v(0, 67.5) * mm, "end": v(-56.15, 48.18) * mm});
            skArc(sketch, "E79.13", {"start": v(60, 40.3) * mm, "mid": v(58.99, 44.68) * mm, "end": v(56.15, 48.18) * mm});
            skLineSegment(sketch, "E79.14", {"start": v(60, 40.3) * mm, "end": v(60, -40.3) * mm});
            skArc(sketch, "E79.15", {"start": v(56.15, -48.18) * mm, "mid": v(58.99, -44.68) * mm, "end": v(60, -40.3) * mm});
            skArc(sketch, "E79.16", {"start": v(-56.15, -48.18) * mm, "mid": v(0, -67.5) * mm, "end": v(56.15, -48.18) * mm});
            skArc(sketch, "E79.17", {"start": v(-60, -40.3) * mm, "mid": v(-58.99, -44.68) * mm, "end": v(-56.15, -48.18) * mm});
            skLineSegment(sketch, "E79.18", {"start": v(-60, 40.3) * mm, "end": v(-60, -40.3) * mm});
            skArc(sketch, "E79.19", {"start": v(-56.15, 48.18) * mm, "mid": v(-58.99, 44.68) * mm, "end": v(-60, 40.3) * mm});
            skLineSegment(sketch, "E80", {"start": v(0, 90) * mm, "end": v(0, 120) * mm, "construction": true});
            skPoint(sketch, "E80.endSnap0", {"position": v(0, 90) * mm});
            skCircle(sketch, "E81", {"center": v(0, 120) * mm, "radius": 6 * mm});
            skLineSegment(sketch, "E82", {"start": v(-33, 90) * mm, "end": v(-15, 108) * mm});
            skLineSegment(sketch, "E83", {"start": v(-15, 108) * mm, "end": v(-15, 120) * mm});
            skLineSegment(sketch, "E84", {"start": v(33, 90) * mm, "end": v(15, 108) * mm});
            skLineSegment(sketch, "E85", {"start": v(15, 108) * mm, "end": v(15, 120) * mm});
            skArc(sketch, "E86", {"start": v(15, 120) * mm, "mid": v(0, 135) * mm, "end": v(-15, 120) * mm});
            skLineSegment(sketch, "E87", {"start": v(-80, 0) * mm, "end": v(80, 0) * mm, "construction": true});
            skLineSegment(sketch, "E88.MirrorCS", {"start": v(15, -108) * mm, "end": v(15, -120) * mm});
            skArc(sketch, "E89.MirrorCS", {"start": v(15, -120) * mm, "mid": v(0, -135) * mm, "end": v(-15, -120) * mm});
            skPoint(sketch, "E90.MirrorP", {"position": v(0, -90) * mm});
            skCircle(sketch, "E91.MirrorC", {"center": v(0, -120) * mm, "radius": 6 * mm});
            skLineSegment(sketch, "E92.MirrorCS", {"start": v(33, -90) * mm, "end": v(15, -108) * mm});
            skLineSegment(sketch, "E93.MirrorCS", {"start": v(-15, -108) * mm, "end": v(-15, -120) * mm});
            skLineSegment(sketch, "E94.MirrorCS", {"start": v(0, -90) * mm, "end": v(0, -120) * mm, "construction": true});
            skLineSegment(sketch, "E95.MirrorCS", {"start": v(-33, -90) * mm, "end": v(-15, -108) * mm});
            skSolve(sketch);
        }
        {
            var Q0;
            {var subQ4=sQuery(id+"F16.wireOp",EDGE,"E79.1");Q0=makeQuery(id+"F16.imprint","IMPRINT",FACE,{"disambiguationData":[TD([[makeQuery(id+"F16.imprint","IMPRINT",EDGE,{"derivedFrom":subQ4}),1.0]])]});}
            var Q1;
            Q1=makeQuery(id+"F16.imprint","IMPRINT",FACE,{"disambiguationData":[TD([[makeQuery(id+"F16.imprint","IMPRINT",EDGE,{"derivedFrom":sQuery(id+"F16.wireOp",EDGE,"E81")}),-1.0]])]});
            var Q2;
            Q2=makeQuery(id+"F16.imprint","IMPRINT",FACE,{"disambiguationData":[TD([[makeQuery(id+"F16.imprint","IMPRINT",EDGE,{"derivedFrom":sQuery(id+"F16.wireOp",EDGE,"E88.MirrorCS")}),-1.0]])]});
            var Q3;
            Q3=makeQuery(id+"F2.opExtrude","CAP_FACE",FACE,{"disambiguationData":[OSD([sQuery(id+"F0.wireOp",EDGE,"E12"),sQuery(id+"F0.wireOp",EDGE,"E13"),sQuery(id+"F0.wireOp",EDGE,"E14"),sQuery(id+"F0.wireOp",EDGE,"E15"),sQuery(id+"F0.wireOp",EDGE,"E17.filletArc"),sQuery(id+"F0.wireOp",EDGE,"E18.filletArc"),sQuery(id+"F0.wireOp",EDGE,"E19.filletArc"),sQuery(id+"F0.wireOp",EDGE,"E20.filletArc"),sQuery(id+"F0.wireOp",EDGE,"E25.0"),sQuery(id+"F0.wireOp",EDGE,"E25.1"),sQuery(id+"F0.wireOp",EDGE,"E25.2"),sQuery(id+"F0.wireOp",EDGE,"E25.3"),sQuery(id+"F0.wireOp",EDGE,"E25.4"),sQuery(id+"F0.wireOp",EDGE,"E25.5"),sQuery(id+"F0.wireOp",EDGE,"E25.6"),sQuery(id+"F0.wireOp",EDGE,"E25.7")])],"isStart":false});
            extrude(context, id + "F17", {"entities" : qUnion([Q0, Q1, Q2]), "endBound" : BoundingType.UP_TO_SURFACE, "endBoundEntityFace" : qUnion([Q3]), "depth" : 25 * mm});
        }
    });
